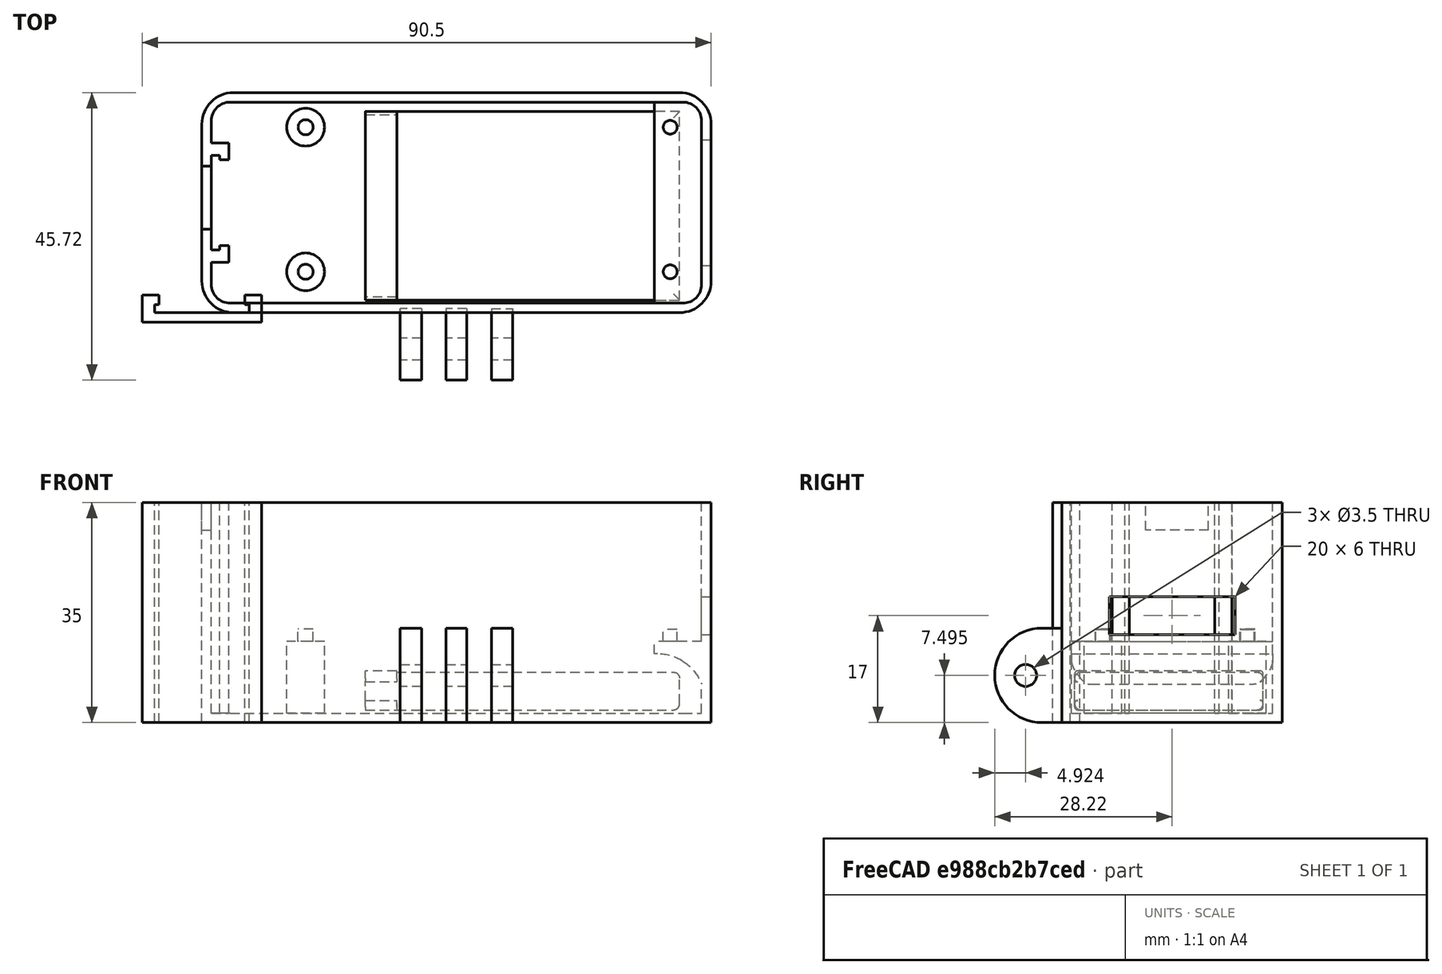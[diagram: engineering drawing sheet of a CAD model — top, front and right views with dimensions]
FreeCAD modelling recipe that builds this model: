
FCSTD DOCUMENT  (FreeCAD 0.16R6712 (Git))
Label: CajaRaspberry
License: CreativeCommons Attribution-ShareAlike
LicenseURL: http://creativecommons.org/licenses/by-sa/4.0/
objects: Part::MultiFuse×8, Part::Box×5, Part::Cylinder×4, Part::Fillet×3, Part::Feature×3, Mesh::Feature×2, Part::Cut×2, Part::Thickness×1, Sketcher::SketchObject×1, PartDesign::Pad×1
note: 29 computed .brp shape members not serialized (recipe doc carries the construction recipe); baked Part::Feature solids carry a one-line shape summary decoded from their .brp

FEATURE [Part::Box] Box  label="Cubo"
  Height = 35
  Length = 81
  Width = 35
FEATURE [Part::Thickness] Thickness
  Faces = -> Box [Face6]
  Intersection = false
  Join = 2
  Mode = 0
  SelfIntersection = false
  Value = -1.5
FEATURE [Mesh::Feature] RaspberryPiZeroW
  Placement = pos=(13,33,13) rot=(1,0,0;1.5708rad)
FEATURE [Mesh::Feature] miTapacajaRaspi
FEATURE [Part::MultiFuse] Fusion  label="Bateria"
  Placement = pos=(26,2,2) rot=(0,0,1;0rad)
FEATURE [Part::Box] Box001  label="Cubo001"
  Height = 2
  Length = 8
  Placement = pos=(72,1,9) rot=(0,0,1;0rad)
  Width = 33
FEATURE [Part::Box] Box002  label="Cubo002"
  Height = 10
  Length = 0.9
  Placement = pos=(80,1,1) rot=(0,0,1;0rad)
  Width = 33
FEATURE [Part::MultiFuse] Fusion001
  Shapes = -> [Box001,Box002]
FEATURE [Part::Fillet] Fillet
  Base = -> Fusion001
  Edges = 1 edges r=7.5: [Edge12]
FEATURE [Part::Cylinder] Cylinder  label="Cilindro"
  Angle = 360
  Height = 12
  Placement = pos=(16.1,6.2,0.9) rot=(0,0,1;0rad)
  Radius = 3
FEATURE [Part::Cylinder] Cylinder001  label="Cilindro001"
  Angle = 360
  Height = 10
  Placement = pos=(16.1,6.2,4.9) rot=(0,0,1;0rad)
  Radius = 1.2
FEATURE [Part::MultiFuse] Fusion002
  Placement = pos=(0.4,23.3,0) rot=(0,0,1;0rad)
  Shapes = -> [Cylinder,Cylinder001]
FEATURE [Part::MultiFuse] Fusion003
  Placement = pos=(0.4,0.3,0) rot=(0,0,1;0rad)
  Shapes = -> [Cylinder,Cylinder001]
FEATURE [Part::Cylinder] Cylinder002  label="Cilindro002"
  Angle = 360
  Height = 3
  Placement = pos=(74.5,6.5,9.9) rot=(0,0,1;0rad)
  Radius = 1.1
FEATURE [Part::Cylinder] Cylinder003  label="Cilindro003"
  Angle = 360
  Height = 3
  Placement = pos=(74.5,29.5,9.9) rot=(0,0,1;0rad)
  Radius = 1.1
FEATURE [Part::MultiFuse] Fusion004
  Placement = pos=(0,0,1.9) rot=(0,0,1;0rad)
  Shapes = -> [Fillet,Cylinder002,Cylinder003]
FEATURE [Part::MultiFuse] Fusion005
  Shapes = -> [Fusion004,Fusion003,Fusion002,Thickness]
FEATURE [Part::Box] Box003  label="Cubo003"
  Height = 6
  Length = 10
  Placement = pos=(77,7.5,14) rot=(0,0,1;0rad)
  Width = 20
FEATURE [Part::Fillet] Fillet001
  Base = -> Fusion005
  Edges = 6 edges r=3: [Edge18,Edge19,Edge21,Edge26,Edge28,Edge30]
FEATURE [Part::Fillet] Fillet002
  Base = -> Fillet001
  Edges = 4 edges r=5: [Edge39,Edge40,Edge43,Edge44]
FEATURE [Part::Cut] Cut
  Base = -> Fillet002
  Tool = -> Box003
FEATURE [Part::Feature] Fusion006
  Placement = pos=(31.55,7,20.1861) rot=(1,0,0;1.5708rad)
  shape: bbox 23 x 11.72 x 35 mm, 27 faces (baked)
FEATURE [Part::MultiFuse] Fusion007  label="miBotCase"
  Shapes = -> [Fusion006,Cut]
FEATURE [Sketcher::SketchObject] Sketch
  sketch-geometry (12):
    g0: LineSegment StartX=-7.5 StartY=0 StartZ=0 EndX=-7.5 EndY=1.3 EndZ=0
    g1: LineSegment StartX=-7.5 StartY=1.3 StartZ=0 EndX=-6.8 EndY=1.3 EndZ=0
    g2: LineSegment StartX=-6.8 StartY=1.3 StartZ=0 EndX=-6.8 EndY=2.8 EndZ=0
    g3: LineSegment StartX=-6.8 StartY=2.8 StartZ=0 EndX=-9.5 EndY=2.8 EndZ=0
    g4: LineSegment StartX=-9.5 StartY=2.8 StartZ=0 EndX=-9.5 EndY=-1.5 EndZ=0
    g5: LineSegment StartX=-9.5 StartY=-1.5 StartZ=0 EndX=9.5 EndY=-1.5 EndZ=0
    g6: LineSegment StartX=9.5 StartY=-1.5 StartZ=0 EndX=9.5 EndY=2.8 EndZ=0
    g7: LineSegment StartX=9.5 StartY=2.8 StartZ=0 EndX=6.8 EndY=2.8 EndZ=0
    g8: LineSegment StartX=6.8 StartY=2.8 StartZ=0 EndX=6.8 EndY=1.3 EndZ=0
    g9: LineSegment StartX=6.8 StartY=1.3 StartZ=0 EndX=7.5 EndY=1.3 EndZ=0
    g10: LineSegment StartX=7.5 StartY=1.3 StartZ=0 EndX=7.5 EndY=0 EndZ=0
    g11: LineSegment StartX=7.5 StartY=0 StartZ=0 EndX=-7.5 EndY=0 EndZ=0
  constraints (38):
    c: PointOnObject(g0,g-1)
    c: Vertical(g0)
    c: Coincident(g0,g1)
    c: Horizontal(g1)
    c: Coincident(g1,g2)
    c: Vertical(g2)
    c: Coincident(g2,g3)
    c: Coincident(g3,g4)
    c: Vertical(g4)
    c: Coincident(g4,g5)
    c: Horizontal(g5)
    c: Coincident(g5,g6)
    c: Vertical(g6)
    c: Coincident(g6,g7)
    c: Horizontal(g7)
    c: Coincident(g7,g8)
    c: Vertical(g8)
    c: Coincident(g8,g9)
    c: Coincident(g9,g10)
    c: PointOnObject(g10,g-1)
    c: Vertical(g10)
    c: Coincident(g10,g11)
    c: Coincident(g11,g0)
    c: Equal(g4,g6)
    c: Equal(g3,g7)
    c: Equal(g1,g9)
    c: Equal(g2,g8)
    c: Horizontal(g9)
    c: Equal(g10,g0)
    c: Symmetric(g3,g6,g-2)
    c: Symmetric(g2,g7,g-2)
    c: Symmetric(g0,g9,g-2)
    c: DistanceX(g11,g11) = 15
    c: DistanceX(g2,g7) = 13.6
    c: DistanceX(g5,g5) = 19
    c: DistanceY(g0,g0) = 1.3
    c: DistanceY(g2,g2) = 1.5
    c: DistanceY(g4,g4) = 4.3
FEATURE [PartDesign::Pad] Pad  label="Pad_guiaPCB"
  Length = 35
  Length2 = 100
  Sketch = -> Sketch
  Type = 0
FEATURE [Part::Feature] Pad001  label="GuiaPCB"
  Placement = pos=(1.5,17.5,0) rot=(0,0,-1;1.5708rad)
  shape: bbox 4.3 x 19 x 35 mm, 14 faces (baked)
FEATURE [Part::Box] Box004  label="Cubo004"
  Height = 4.95
  Length = 9
  Placement = pos=(-1.7,13.3,30.6) rot=(0,0,1;0rad)
  Width = 10
FEATURE [Part::MultiFuse] Fusion008
  Shapes = -> [Fusion007,Pad001]
FEATURE [Part::Cut] Cut001  label="CajaRasp"
  Base = -> Fusion008
  Tool = -> Box004
FEATURE [Part::Feature] Cut001001  label="csCajaRasp"
  shape: bbox 81 x 45.73 x 35 mm, 89 faces (baked)
